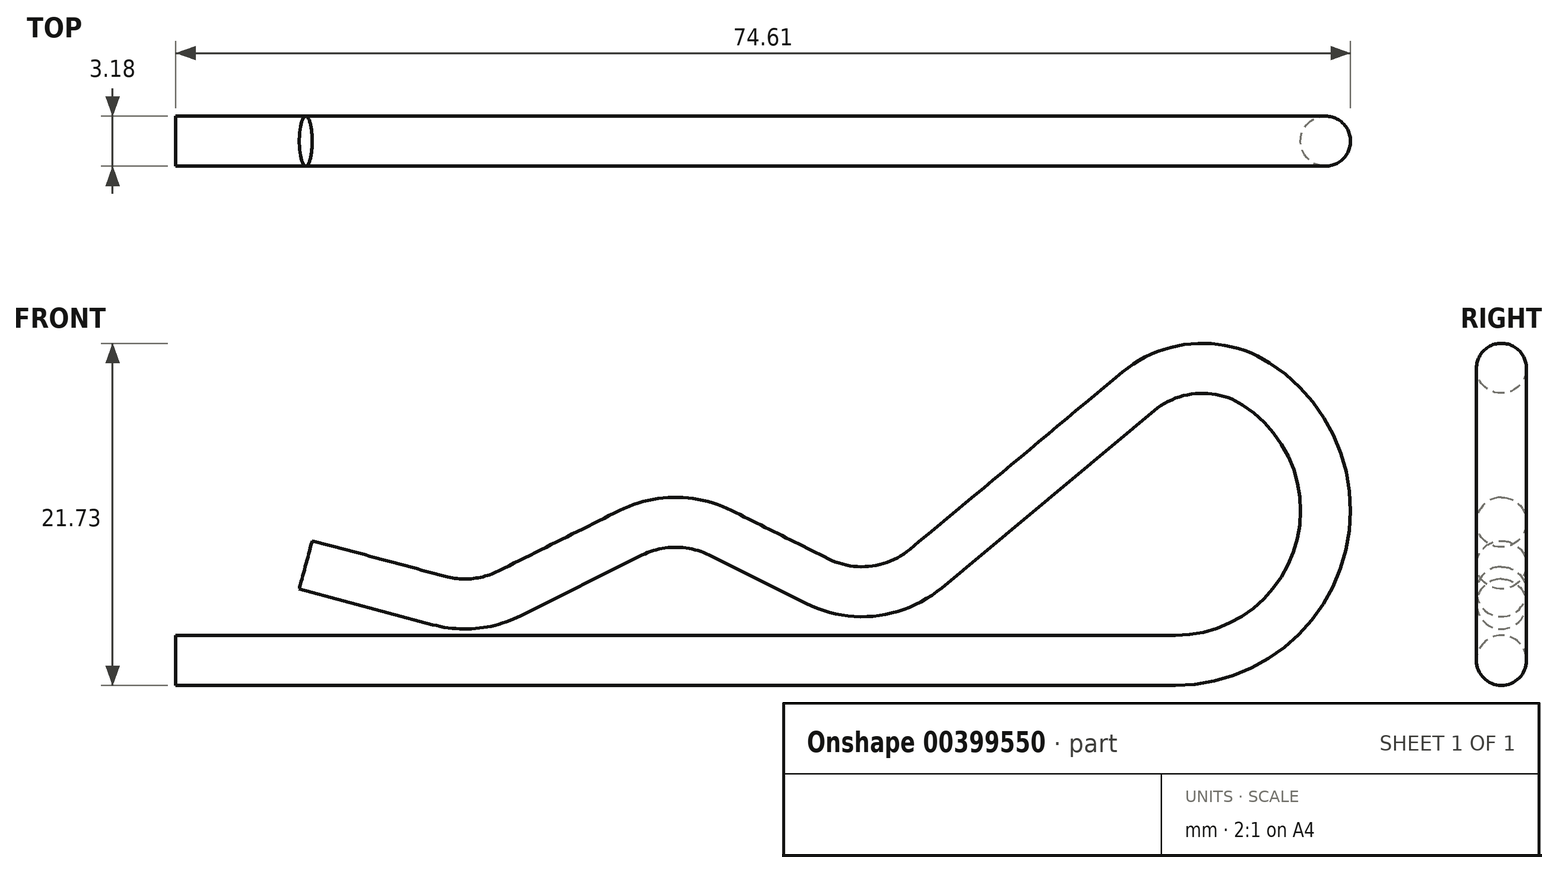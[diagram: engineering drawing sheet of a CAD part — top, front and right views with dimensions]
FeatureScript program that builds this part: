
annotation { "Feature Type Name" : "Feature", "Feature Type Description" : "" }
export const myFeature = defineFeature(function(context is Context, id is Id, definition is map)
    precondition{}
    {
        {
            var Q0;
            Q0=qCreatedBy(makeId("Front.planeOp"),FACE);
            var sketch = newSketch(context, id + "F0", { "sketchPlane" : qUnion([Q0])});
            skLineSegment(sketch, "E0", {"start": v(0, 0) * mm, "end": v(63.5, 0) * mm});
            skLineSegment(sketch, "E1", {"start": v(63.5, 0) * mm, "end": v(63.5, 19.05) * mm, "construction": true});
            skLineSegment(sketch, "E2", {"start": v(61.14, 17.08) * mm, "end": v(47.64, 5.83) * mm});
            skLineSegment(sketch, "E3", {"start": v(40.74, 5.03) * mm, "end": v(34.59, 8.1) * mm});
            skLineSegment(sketch, "E4", {"start": v(28.91, 8.1) * mm, "end": v(21.2, 4.25) * mm});
            skLineSegment(sketch, "E5", {"start": v(16.72, 3.8) * mm, "end": v(8.26, 6.07) * mm});
            skArc(sketch, "E6", {"start": v(63.5, 0) * mm, "mid": v(72.65, 6.86) * mm, "end": v(68.61, 17.56) * mm});
            skPoint(sketch, "E7.visualSharp", {"position": v(44.45, 3.18) * mm});
            skArc(sketch, "E7.filletArc", {"start": v(40.74, 5.03) * mm, "mid": v(44.3, 4.4) * mm, "end": v(47.64, 5.83) * mm});
            skPoint(sketch, "E8.visualSharp", {"position": v(19.05, 3.18) * mm});
            skArc(sketch, "E8.filletArc", {"start": v(16.72, 3.8) * mm, "mid": v(19, 3.61) * mm, "end": v(21.2, 4.25) * mm});
            skPoint(sketch, "E9.visualSharp", {"position": v(31.75, 9.53) * mm});
            skArc(sketch, "E9.filletArc", {"start": v(34.59, 8.1) * mm, "mid": v(31.75, 8.78) * mm, "end": v(28.91, 8.1) * mm});
            skPoint(sketch, "E10.visualSharp", {"position": v(63.5, 19.05) * mm});
            skArc(sketch, "E10.filletArc", {"start": v(68.61, 17.56) * mm, "mid": v(64.8, 18.54) * mm, "end": v(61.14, 17.08) * mm});
            skPoint(sketch, "E11.second.point", {"position": v(54.39, 11.46) * mm});
            skSolve(sketch);
        }
        {
            var Q0;
            Q0=qCreatedBy(makeId("Right.planeOp"),FACE);
            var sketch = newSketch(context, id + "F1", { "sketchPlane" : qUnion([Q0])});
            skCircle(sketch, "E12", {"center": v(0, 0) * mm, "radius": 1.59 * mm});
            skSolve(sketch);
        }
        {
            var Q0;
            Q0=makeQuery(id+"F1.imprint","IMPRINT",FACE,{"disambiguationData":[TD([[makeQuery(id+"F1.imprint","IMPRINT",EDGE,{"derivedFrom":sQuery(id+"F1.wireOp",EDGE,"E12")}),1.0]])]});
            var Q1;
            Q1=sQuery(id+"F0.wireOp",EDGE,"E0");
            var Q2;
            Q2=sQuery(id+"F0.wireOp",EDGE,"E6");
            var Q3;
            Q3=sQuery(id+"F0.wireOp",EDGE,"E10.filletArc");
            var Q4;
            Q4=sQuery(id+"F0.wireOp",EDGE,"E2");
            var Q5;
            Q5=sQuery(id+"F0.wireOp",EDGE,"E7.filletArc");
            var Q6;
            Q6=sQuery(id+"F0.wireOp",EDGE,"E3");
            var Q7;
            Q7=sQuery(id+"F0.wireOp",EDGE,"E9.filletArc");
            var Q8;
            Q8=sQuery(id+"F0.wireOp",EDGE,"E4");
            var Q9;
            Q9=sQuery(id+"F0.wireOp",EDGE,"E8.filletArc");
            var Q10;
            Q10=sQuery(id+"F0.wireOp",EDGE,"E5");
            sweep(context, id + "F2", {"profiles" : qUnion([Q0]), "path" : qUnion([Q1, Q2, Q3, Q4, Q5, Q6, Q7, Q8, Q9, Q10])});
        }
    });
